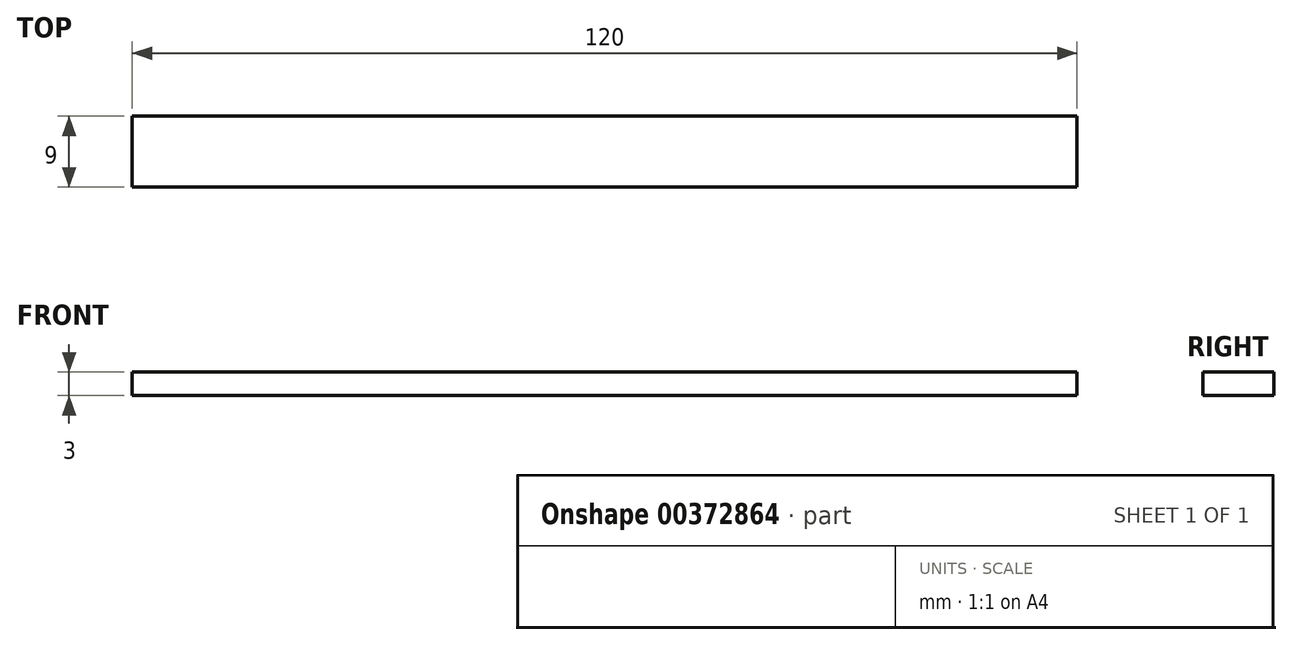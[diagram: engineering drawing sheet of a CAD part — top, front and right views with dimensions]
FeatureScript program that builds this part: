
annotation { "Feature Type Name" : "Feature", "Feature Type Description" : "" }
export const myFeature = defineFeature(function(context is Context, id is Id, definition is map)
    precondition{}
    {
        {
            var Q0;
            Q0=qCreatedBy(makeId("Top.planeOp"),FACE);
            var sketch = newSketch(context, id + "F0", { "sketchPlane" : qUnion([Q0])});
            skLineSegment(sketch, "E0.bottom", {"start": v(-57.98, -5.45) * mm, "end": v(62.02, -5.45) * mm});
            skLineSegment(sketch, "E0.top", {"start": v(-57.98, -14.45) * mm, "end": v(62.02, -14.45) * mm});
            skLineSegment(sketch, "E0.left", {"start": v(-57.98, -5.45) * mm, "end": v(-57.98, -14.45) * mm});
            skLineSegment(sketch, "E0.right", {"start": v(62.02, -5.45) * mm, "end": v(62.02, -14.45) * mm});
            skSolve(sketch);
        }
        {
            var Q0;
            Q0=makeQuery(id+"F0.imprint","IMPRINT",FACE,{"disambiguationData":[TD([[makeQuery(id+"F0.imprint","IMPRINT",EDGE,{"derivedFrom":sQuery(id+"F0.wireOp",EDGE,"E0.bottom")}),-1.0]])]});
            extrude(context, id + "F1", {"entities" : qUnion([Q0]), "depth" : 3 * mm});
        }
    });
